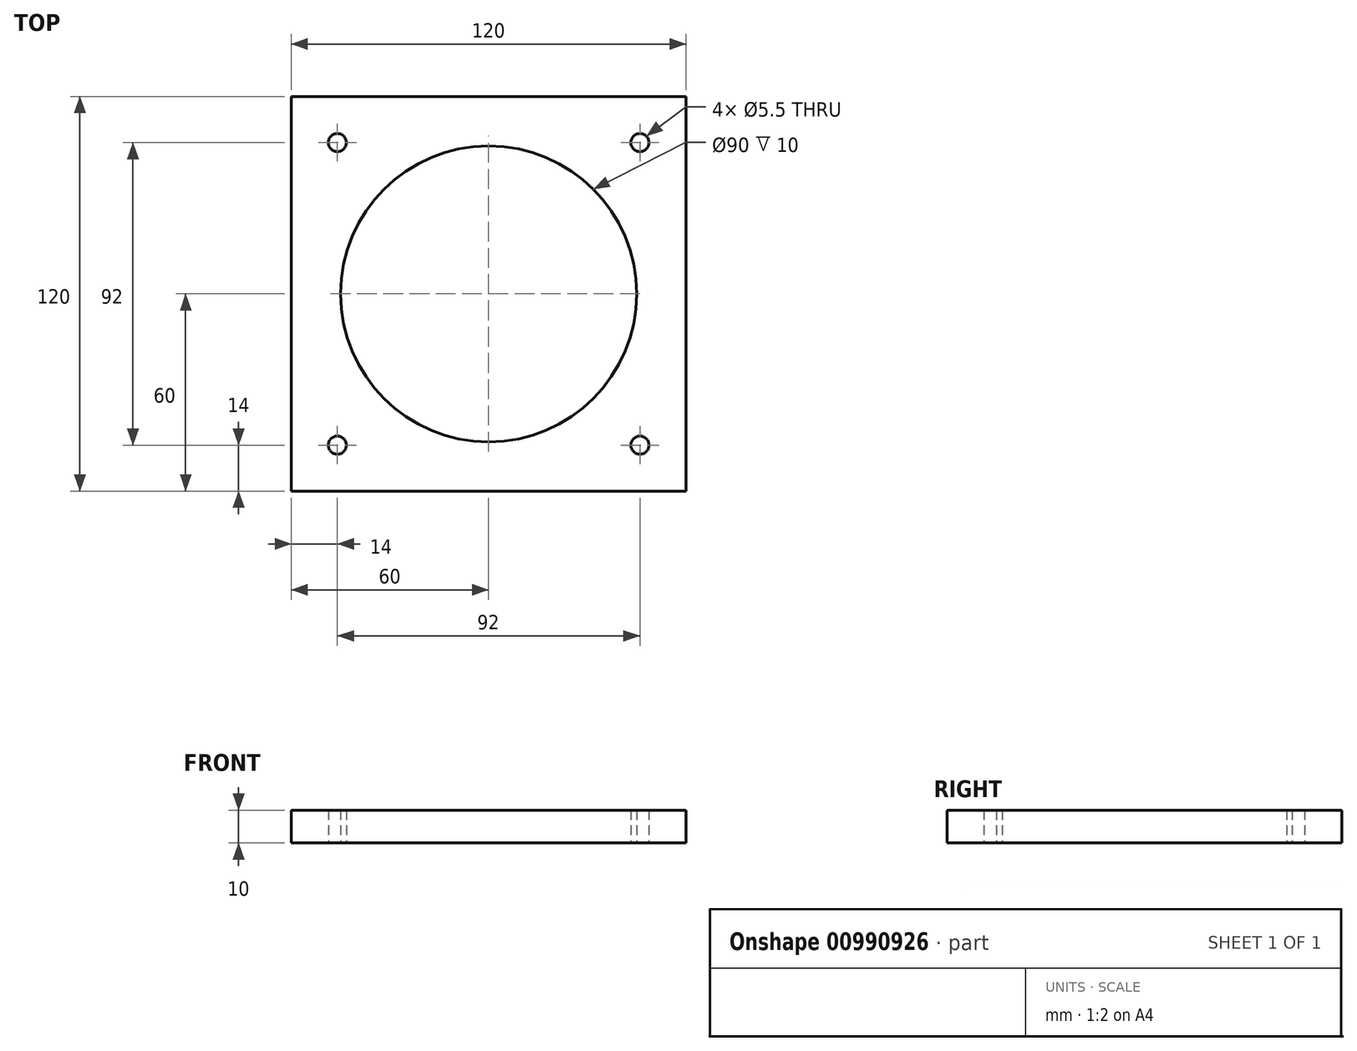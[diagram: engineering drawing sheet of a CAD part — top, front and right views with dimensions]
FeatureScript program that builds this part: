
annotation { "Feature Type Name" : "Feature", "Feature Type Description" : "" }
export const myFeature = defineFeature(function(context is Context, id is Id, definition is map)
    precondition{}
    {
        {
            var Q0;
            Q0=qCreatedBy(makeId("Top.planeOp"),FACE);
            var sketch = newSketch(context, id + "F0", { "sketchPlane" : qUnion([Q0])});
            skLineSegment(sketch, "E0.bottom", {"start": v(60, -60) * mm, "end": v(-60, -60) * mm});
            skLineSegment(sketch, "E0.top", {"start": v(60, 60) * mm, "end": v(-60, 60) * mm});
            skLineSegment(sketch, "E0.left", {"start": v(60, -60) * mm, "end": v(60, 60) * mm});
            skLineSegment(sketch, "E0.right", {"start": v(-60, -60) * mm, "end": v(-60, 60) * mm});
            skPoint(sketch, "E0.middle", {"position": v(0, 0) * mm});
            skCircle(sketch, "E1", {"center": v(0, 0) * mm, "radius": 20 * mm});
            skLineSegment(sketch, "E2", {"start": v(20, 0) * mm, "end": v(60, 0) * mm, "construction": true});
            skLineSegment(sketch, "E3", {"start": v(0, -20) * mm, "end": v(0, -60) * mm, "construction": true});
            skCircle(sketch, "E4", {"center": v(-46, 46) * mm, "radius": 2.75 * mm});
            skCircle(sketch, "E5.MirrorC", {"center": v(46, 46) * mm, "radius": 2.75 * mm});
            skCircle(sketch, "E6.MirrorC", {"center": v(-46, -46) * mm, "radius": 2.75 * mm});
            skCircle(sketch, "E7.MirrorC", {"center": v(46, -46) * mm, "radius": 2.75 * mm});
            skCircle(sketch, "E8", {"center": v(-18.38, 18.38) * mm, "radius": 2.75 * mm});
            skCircle(sketch, "E9.MirrorC", {"center": v(18.38, 18.38) * mm, "radius": 2.75 * mm});
            skCircle(sketch, "E10.MirrorC", {"center": v(-18.38, -18.38) * mm, "radius": 2.75 * mm});
            skCircle(sketch, "E11.MirrorC", {"center": v(18.38, -18.38) * mm, "radius": 2.75 * mm});
            skCircle(sketch, "E12", {"center": v(0, 0) * mm, "radius": 26 * mm, "construction": true});
            skCircle(sketch, "E13", {"center": v(0, 0) * mm, "radius": 45 * mm});
            skCircle(sketch, "E14", {"center": v(0, 0) * mm, "radius": 35 * mm});
            skLineSegment(sketch, "E15", {"start": v(-46, 46) * mm, "end": v(46, -46) * mm, "construction": true});
            skLineSegment(sketch, "E16", {"start": v(-46, -46) * mm, "end": v(46, 46) * mm, "construction": true});
            skLineSegment(sketch, "E17.left", {"start": v(-4.68, 44.76) * mm, "end": v(-4.68, 34.69) * mm});
            skLineSegment(sketch, "E17.right", {"start": v(4.68, 44.76) * mm, "end": v(4.68, 34.69) * mm});
            skSolve(sketch);
        }
        {
            var Q0;
            Q0 = qSketchRegion(id + "F0", true);
            extrude(context, id + "F1", {"entities" : qUnion([Q0]), "depth" : 10 * mm, "offsetDistance" : 25 * mm});
        }
    });
